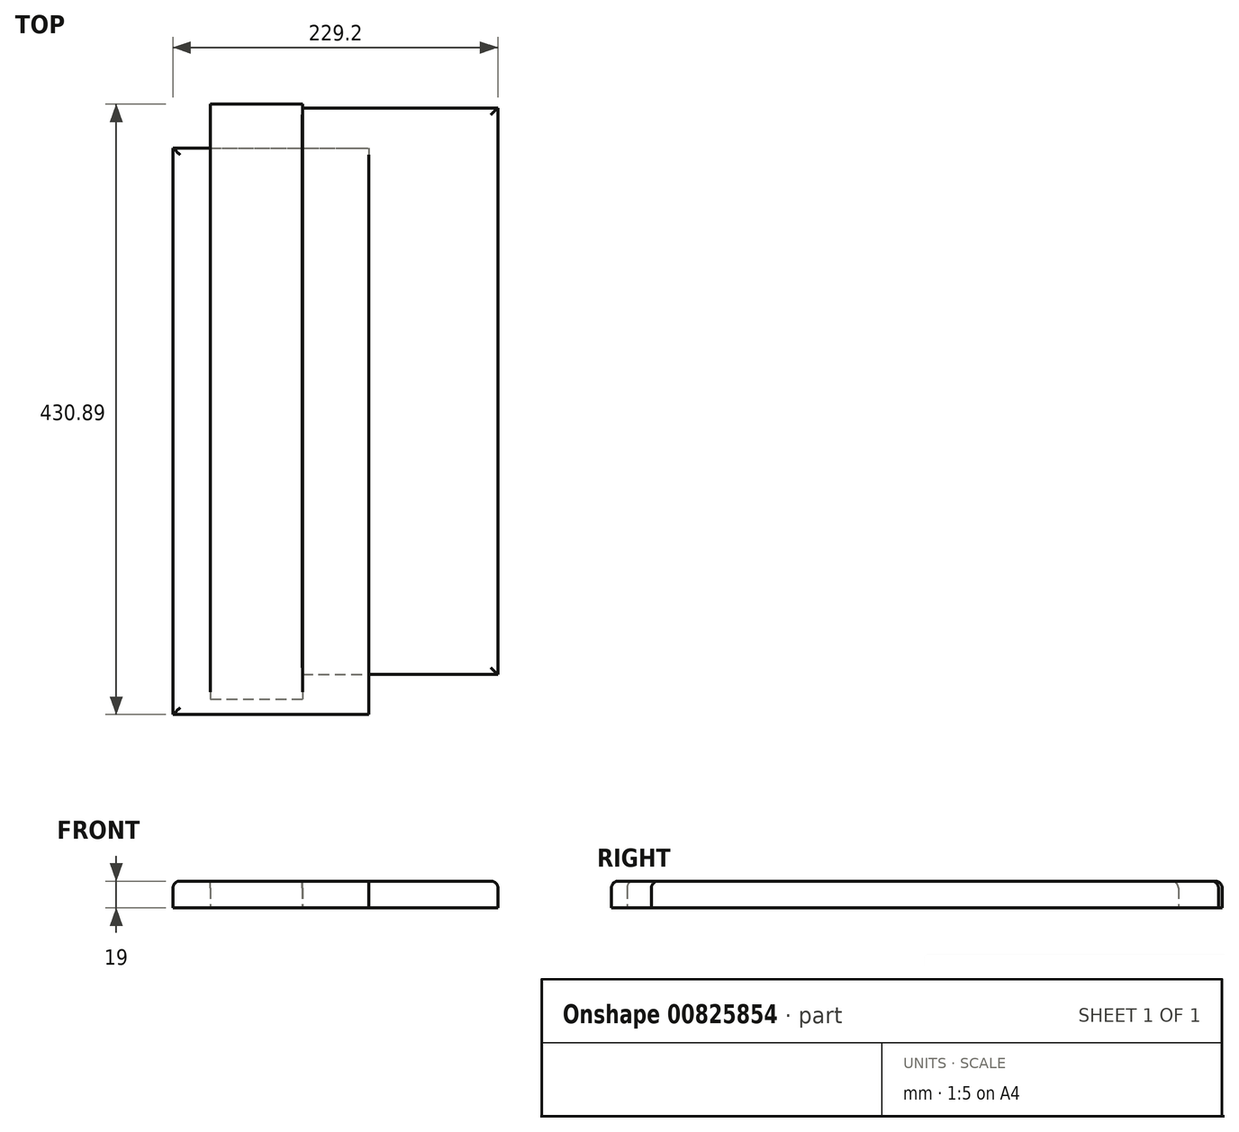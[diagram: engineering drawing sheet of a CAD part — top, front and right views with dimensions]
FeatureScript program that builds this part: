
annotation { "Feature Type Name" : "Feature", "Feature Type Description" : "" }
export const myFeature = defineFeature(function(context is Context, id is Id, definition is map)
    precondition{}
    {
        {
            var Q0;
            Q0=qCreatedBy(makeId("Top.planeOp"),FACE);
            var sketch = newSketch(context, id + "F0", { "sketchPlane" : qUnion([Q0])});
            skLineSegment(sketch, "E0.bottom", {"start": v(-111.58, 211.7) * mm, "end": v(-46.58, 211.7) * mm});
            skLineSegment(sketch, "E0.top", {"start": v(-111.58, -208.17) * mm, "end": v(-46.58, -208.17) * mm});
            skLineSegment(sketch, "E0.left", {"start": v(-111.58, 211.7) * mm, "end": v(-111.58, -208.17) * mm});
            skLineSegment(sketch, "E0.right", {"start": v(-46.58, 211.7) * mm, "end": v(-46.58, -208.17) * mm});
            skSolve(sketch);
        }
        {
            var Q0;
            Q0=qCreatedBy(makeId("Top.planeOp"),FACE);
            var sketch = newSketch(context, id + "F1", { "sketchPlane" : qUnion([Q0])});
            skLineSegment(sketch, "E1.bottom", {"start": v(-138, 180.81) * mm, "end": v(0, 180.81) * mm});
            skLineSegment(sketch, "E1.top", {"start": v(-138, -219.19) * mm, "end": v(0, -219.19) * mm});
            skLineSegment(sketch, "E1.left", {"start": v(-138, 180.81) * mm, "end": v(-138, -219.19) * mm});
            skLineSegment(sketch, "E1.right", {"start": v(0, 180.81) * mm, "end": v(0, -219.19) * mm});
            skSolve(sketch);
        }
        {
            var Q0;
            Q0=qCreatedBy(makeId("Top.planeOp"),FACE);
            var sketch = newSketch(context, id + "F2", { "sketchPlane" : qUnion([Q0])});
            skLineSegment(sketch, "E2.bottom", {"start": v(-46.8, 209.09) * mm, "end": v(91.2, 209.09) * mm});
            skLineSegment(sketch, "E2.top", {"start": v(-46.8, -190.91) * mm, "end": v(91.2, -190.91) * mm});
            skLineSegment(sketch, "E2.left", {"start": v(-46.8, 209.09) * mm, "end": v(-46.8, -190.91) * mm});
            skLineSegment(sketch, "E2.right", {"start": v(91.2, 209.09) * mm, "end": v(91.2, -190.91) * mm});
            skSolve(sketch);
        }
        {
            var Q0;
            Q0=makeQuery(id+"F2.imprint","IMPRINT",FACE,{"disambiguationData":[TD([[makeQuery(id+"F2.imprint","IMPRINT",EDGE,{"derivedFrom":sQuery(id+"F2.wireOp",EDGE,"E2.bottom")}),-1.0]])]});
            var Q1;
            Q1=makeQuery(id+"F0.imprint","IMPRINT",FACE,{"disambiguationData":[TD([[makeQuery(id+"F0.imprint","IMPRINT",EDGE,{"derivedFrom":sQuery(id+"F0.wireOp",EDGE,"E0.bottom")}),-1.0]])]});
            var Q2;
            Q2=makeQuery(id+"F1.imprint","IMPRINT",FACE,{"disambiguationData":[TD([[makeQuery(id+"F1.imprint","IMPRINT",EDGE,{"derivedFrom":sQuery(id+"F1.wireOp",EDGE,"E1.bottom")}),-1.0]])]});
            extrude(context, id + "F3", {"entities" : qUnion([Q0, Q1, Q2]), "depth" : 19 * mm, "offsetDistance" : 25 * mm});
        }
        {
            var Q0;
            Q0=makeQuery(id+"F3.opExtrude","CAP_EDGE",EDGE,{"disambiguationData":[OSD([sQuery(id+"F1.wireOp",EDGE,"E1.left")])],"isStart":false});
            var Q1;
            Q1=makeQuery(id+"F3.opExtrude","CAP_EDGE",EDGE,{"disambiguationData":[OSD([sQuery(id+"F1.wireOp",EDGE,"E1.top")])],"isStart":false});
            var Q2;
            Q2=makeQuery(id+"F3.opExtrude","CAP_EDGE",EDGE,{"disambiguationData":[OSD([sQuery(id+"F0.wireOp",EDGE,"E0.top")])],"isStart":false});
            var Q3;
            Q3=makeQuery(id+"F3.opExtrude","CAP_EDGE",EDGE,{"disambiguationData":[OSD([sQuery(id+"F2.wireOp",EDGE,"E2.top")])],"isStart":false});
            var Q4;
            Q4=makeQuery(id+"F3.opExtrude","CAP_EDGE",EDGE,{"disambiguationData":[OSD([sQuery(id+"F2.wireOp",EDGE,"E2.right")])],"isStart":false});
            var Q5;
            Q5=makeQuery(id+"F3.opExtrude","CAP_EDGE",EDGE,{"disambiguationData":[OSD([sQuery(id+"F2.wireOp",EDGE,"E2.bottom")])],"isStart":false});
            var Q6;
            Q6=makeQuery(id+"F3.opExtrude","CAP_EDGE",EDGE,{"disambiguationData":[OSD([sQuery(id+"F1.wireOp",EDGE,"E1.bottom")])],"isStart":false});
            var Q7;
            Q7=makeQuery(id+"F3.opExtrude","CAP_EDGE",EDGE,{"disambiguationData":[OSD([sQuery(id+"F0.wireOp",EDGE,"E0.bottom")])],"isStart":false});
            fillet(context, id + "F4", {"entities" : qUnion([Q0, Q1, Q2, Q3, Q4, Q5, Q6, Q7]), "radius" : 5 * mm, "tangentPropagation" : true, "allowEdgeOverflow" : false});
        }
    });
